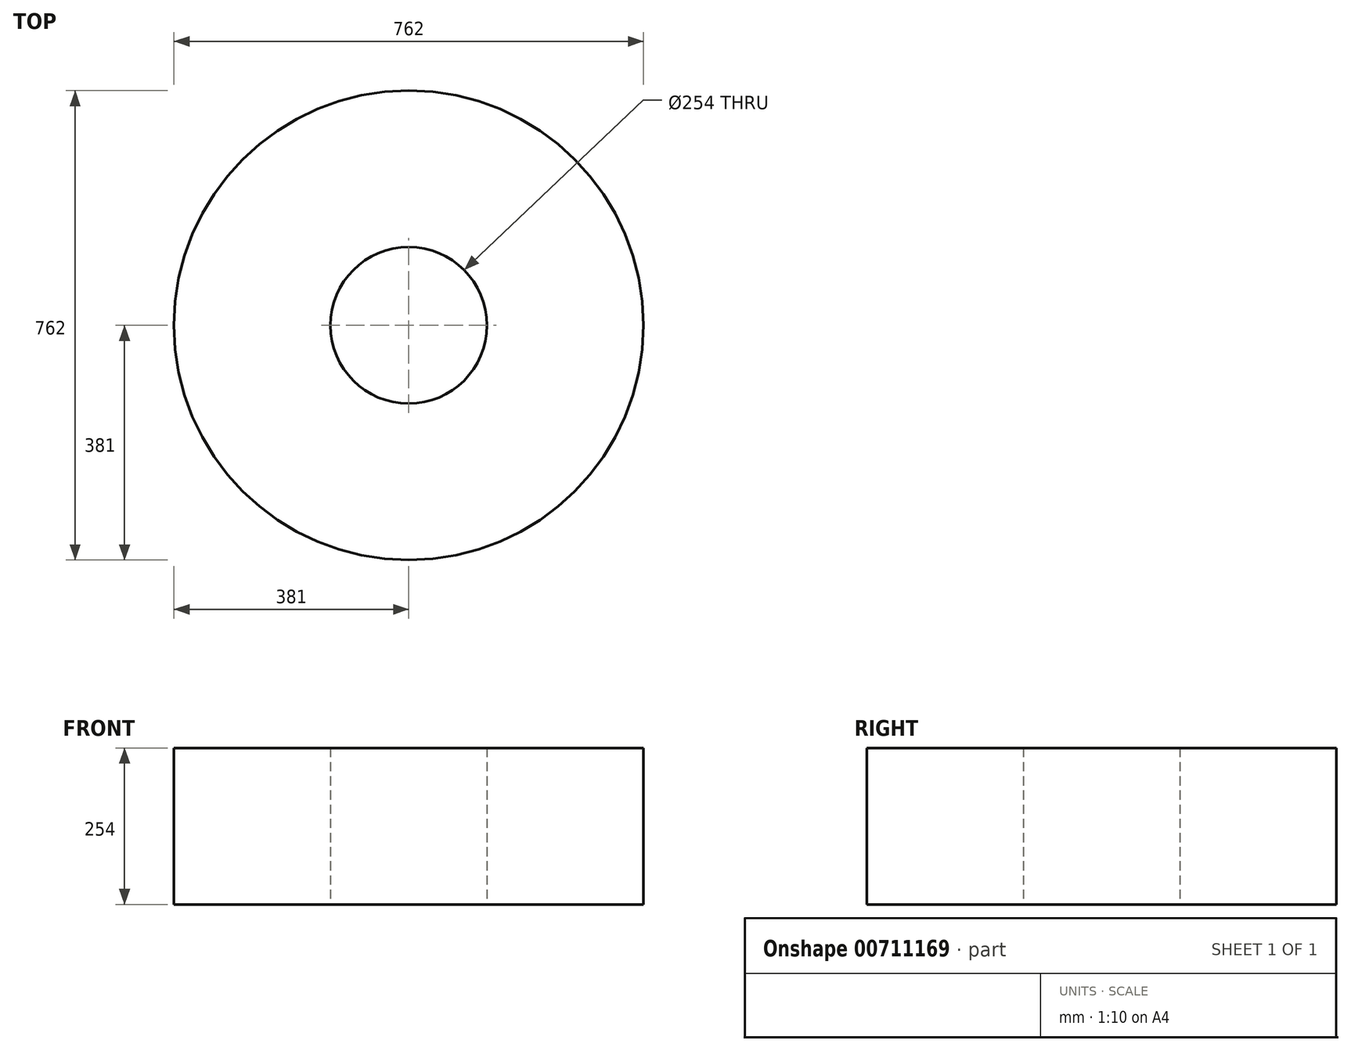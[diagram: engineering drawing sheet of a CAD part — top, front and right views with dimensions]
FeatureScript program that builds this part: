
annotation { "Feature Type Name" : "Feature", "Feature Type Description" : "" }
export const myFeature = defineFeature(function(context is Context, id is Id, definition is map)
    precondition{}
    {
        {
            var Q0;
            Q0=qCreatedBy(makeId("Top.planeOp"),FACE);
            var sketch = newSketch(context, id + "F0", { "sketchPlane" : qUnion([Q0])});
            skLineSegment(sketch, "E0", {"start": v(0, 0) * mm, "end": v(170.68, 0) * mm, "construction": true});
            skLineSegment(sketch, "E1", {"start": v(0, 0) * mm, "end": v(0, 105.54) * mm, "construction": true});
            skCircle(sketch, "E2", {"center": v(0, 0) * mm, "radius": 381 * mm});
            skCircle(sketch, "E3", {"center": v(0, 0) * mm, "radius": 127 * mm});
            skSolve(sketch);
        }
        {
            var Q0;
            Q0 = qSketchRegion(id + "F0", true);
            extrude(context, id + "F1", {"entities" : qUnion([Q0]), "depth" : 254 * mm, "offsetDistance" : 25.4 * mm});
        }
    });
